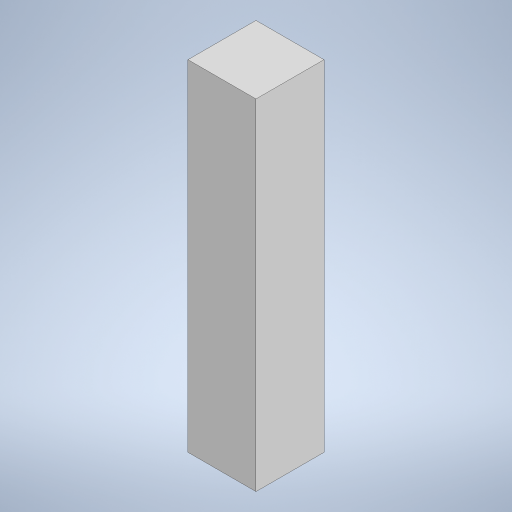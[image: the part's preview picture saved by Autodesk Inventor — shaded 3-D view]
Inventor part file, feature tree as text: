
AUTODESK INVENTOR PART (.ipt)
format: ipt  version: 2023 (Build 270158000, 158)  size: 209,920 bytes
history: native  units: mm
features: extrude x1, sketch x1
ambient origin geometry x8: Origin, YZ Plane, XZ Plane, XY Plane, X Axis, Y Axis, Z Axis, Center Point
bodies: Solid1 (feature_tree)
feature tree (2):
  extrude  "Extrusion1"  Depth=5.0mm
  sketch  "Sketch1"  dims[d0=5.0mm d1=5.0mm d2=25.0mm d3=0.0mm]
